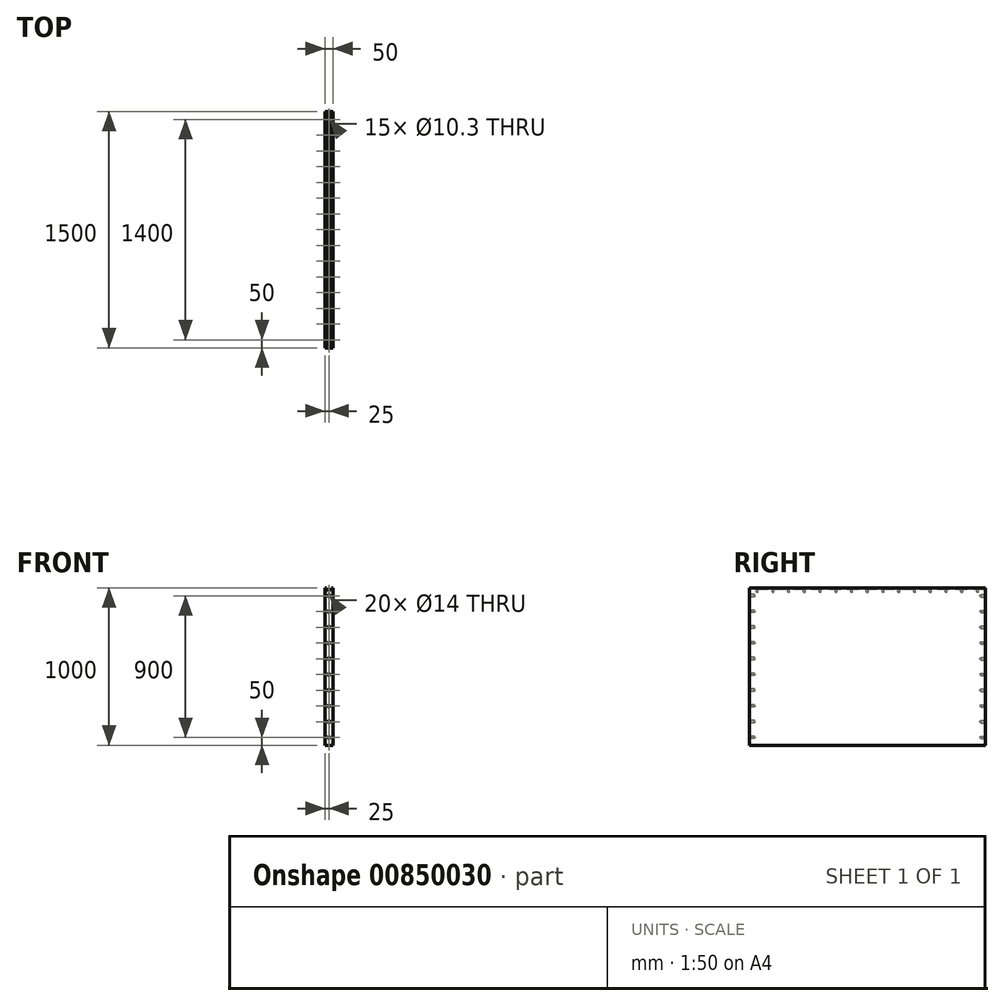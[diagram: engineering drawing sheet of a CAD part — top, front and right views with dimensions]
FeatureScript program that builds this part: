
annotation { "Feature Type Name" : "Feature", "Feature Type Description" : "" }
export const myFeature = defineFeature(function(context is Context, id is Id, definition is map)
    precondition{}
    {
        {
            var Q0;
            Q0=qCreatedBy(makeId("Right.planeOp"),FACE);
            var sketch = newSketch(context, id + "F0", { "sketchPlane" : qUnion([Q0])});
            skLineSegment(sketch, "E0.bottom", {"start": v(750, 500) * mm, "end": v(-750, 500) * mm});
            skLineSegment(sketch, "E0.top", {"start": v(750, -500) * mm, "end": v(-750, -500) * mm});
            skLineSegment(sketch, "E0.left", {"start": v(750, 500) * mm, "end": v(750, -500) * mm});
            skLineSegment(sketch, "E0.right", {"start": v(-750, 500) * mm, "end": v(-750, -500) * mm});
            skPoint(sketch, "E0.middle", {"position": v(0, 0) * mm});
            skSolve(sketch);
        }
        {
            var Q0;
            Q0=makeQuery(id+"F0.imprint","IMPRINT",FACE,{"disambiguationData":[TD([[makeQuery(id+"F0.imprint","IMPRINT",EDGE,{"derivedFrom":sQuery(id+"F0.wireOp",EDGE,"E0.bottom")}),1.0]])]});
            extrude(context, id + "F1", {"entities" : qUnion([Q0]), "depth" : 50 * mm, "offsetDistance" : 25 * mm});
        }
        {
            var Q0;
            Q0=makeQuery(id+"F1.opExtrude","SWEPT_FACE",FACE,{"disambiguationData":[OSD([sQuery(id+"F0.wireOp",EDGE,"E0.bottom")])]});
            var sketch = newSketch(context, id + "F2", { "sketchPlane" : qUnion([Q0])});
            skCircle(sketch, "E1", {"center": v(25, -700) * mm, "radius": 5.25 * mm});
            skCircle(sketch, "E2.0.1.0", {"center": v(25, -600) * mm, "radius": 5.25 * mm});
            skCircle(sketch, "E2.0.2.0", {"center": v(25, -500) * mm, "radius": 5.25 * mm});
            skCircle(sketch, "E2.0.3.0", {"center": v(25, -400) * mm, "radius": 5.25 * mm});
            skCircle(sketch, "E2.0.4.0", {"center": v(25, -300) * mm, "radius": 5.25 * mm});
            skCircle(sketch, "E2.0.5.0", {"center": v(25, -200) * mm, "radius": 5.25 * mm});
            skCircle(sketch, "E2.0.6.0", {"center": v(25, -100) * mm, "radius": 5.25 * mm});
            skCircle(sketch, "E2.0.7.0", {"center": v(25, 0) * mm, "radius": 5.25 * mm});
            skCircle(sketch, "E2.0.8.0", {"center": v(25, 100) * mm, "radius": 5.25 * mm});
            skCircle(sketch, "E2.0.9.0", {"center": v(25, 200) * mm, "radius": 5.25 * mm});
            skCircle(sketch, "E2.0.10.0", {"center": v(25, 300) * mm, "radius": 5.25 * mm});
            skCircle(sketch, "E2.0.11.0", {"center": v(25, 400) * mm, "radius": 5.25 * mm});
            skCircle(sketch, "E2.0.12.0", {"center": v(25, 500) * mm, "radius": 5.25 * mm});
            skCircle(sketch, "E2.0.13.0", {"center": v(25, 600) * mm, "radius": 5.25 * mm});
            skCircle(sketch, "E2.0.14.0", {"center": v(25, 700) * mm, "radius": 5.25 * mm});
            skLineSegment(sketch, "E2.direction1", {"start": v(25, -700) * mm, "end": v(50, -700) * mm, "construction": true});
            skLineSegment(sketch, "E2.direction2", {"start": v(25, -700) * mm, "end": v(25, -600) * mm, "construction": true});
            skSolve(sketch);
        }
        {
            var Q0;
            Q0=sQuery(id+"F2.wireOp",VERTEX,"E1.center");
            var Q1;
            Q1=sQuery(id+"F2.wireOp",VERTEX,"E2.0.1.0.center");
            var Q2;
            Q2=sQuery(id+"F2.wireOp",VERTEX,"E2.0.2.0.center");
            var Q3;
            Q3=sQuery(id+"F2.wireOp",VERTEX,"E2.0.3.0.center");
            var Q4;
            Q4=sQuery(id+"F2.wireOp",VERTEX,"E2.0.4.0.center");
            var Q5;
            Q5=sQuery(id+"F2.wireOp",VERTEX,"E2.0.5.0.center");
            var Q6;
            Q6=sQuery(id+"F2.wireOp",VERTEX,"E2.0.6.0.center");
            var Q7;
            Q7=sQuery(id+"F2.wireOp",VERTEX,"E2.0.7.0.center");
            var Q8;
            Q8=sQuery(id+"F2.wireOp",VERTEX,"E2.0.9.0.center");
            var Q9;
            Q9=sQuery(id+"F2.wireOp",VERTEX,"E2.0.8.0.center");
            var Q10;
            Q10=sQuery(id+"F2.wireOp",VERTEX,"E2.0.10.0.center");
            var Q11;
            Q11=sQuery(id+"F2.wireOp",VERTEX,"E2.0.11.0.center");
            var Q12;
            Q12=sQuery(id+"F2.wireOp",VERTEX,"E2.0.12.0.center");
            var Q13;
            Q13=sQuery(id+"F2.wireOp",VERTEX,"E2.0.14.0.center");
            var Q14;
            Q14=sQuery(id+"F2.wireOp",VERTEX,"E2.0.13.0.center");
            var Q15;
            Q15=makeQuery(id+"F1.opExtrude","SWEPT_BODY",BODY,{"disambiguationData":[OSD([sQuery(id+"F0.wireOp",EDGE,"E0.bottom"),sQuery(id+"F0.wireOp",EDGE,"E0.top"),sQuery(id+"F0.wireOp",EDGE,"E0.left"),sQuery(id+"F0.wireOp",EDGE,"E0.right")])]});
            hole(context, id + "F3", {"style" : HoleStyle.SIMPLE, "endStyle" : HoleEndStyle.BLIND, "standardTappedOrClearance" : lookupTablePath({ "standard" : "ISO", "fit" : "Normal", "engagement" : "75%", "pitch" : "1.75 mm", "size" : "M12", "type" : "Tapped" }), "standardBlindInLast" : lookupTablePath({ "fit" : "Standard", "standard" : "ISO", "engagement" : "75%", "pitch" : "1.75 mm", "size" : "M12", "type" : "Tapped" }), "holeDiameter" : 10.3 * mm, "majorDiameter" : 12 * mm, "showTappedDepth" : true, "holeDepth" : 25.25 * mm, "isTappedThrough" : true, "tappedDepth" : 20 * mm, "tapClearance" : 3, "locations" : qUnion([Q0, Q1, Q2, Q3, Q4, Q5, Q6, Q7, Q8, Q9, Q10, Q11, Q12, Q13, Q14]), "scope" : qUnion([Q15])});
        }
        {
            var Q0;
            Q0=makeQuery(id+"F1.opExtrude","SWEPT_FACE",FACE,{"disambiguationData":[OSD([sQuery(id+"F0.wireOp",EDGE,"E0.right")])]});
            var sketch = newSketch(context, id + "F4", { "sketchPlane" : qUnion([Q0])});
            skLineSegment(sketch, "E3.bottom", {"start": v(40, 490) * mm, "end": v(10, 490) * mm});
            skLineSegment(sketch, "E3.top", {"start": v(40, 510) * mm, "end": v(10, 510) * mm});
            skLineSegment(sketch, "E3.left", {"start": v(40, 490) * mm, "end": v(40, 510) * mm});
            skLineSegment(sketch, "E3.right", {"start": v(10, 490) * mm, "end": v(10, 510) * mm});
            skPoint(sketch, "E3.middle", {"position": v(25, 500) * mm});
            skSolve(sketch);
        }
        {
            var Q0;
            {var subQ0=sQuery(id+"F4.wireOp",EDGE,"E3.bottom");Q0=makeQuery(id+"F4.imprint","IMPRINT",FACE,{"disambiguationData":[TD([[makeQuery(id+"F4.imprint","IMPRINT",EDGE,{"derivedFrom":subQ0}),-1.0]])]});}
            extrude(context, id + "F5", {"entities" : qUnion([Q0]), "operationType" : NewBodyOperationType.REMOVE, "endBound" : BoundingType.THROUGH_ALL, "oppositeDirection" : true, "depth" : 25 * mm, "offsetDistance" : 25 * mm});
        }
        {
            var Q0;
            Q0=makeQuery(id+"F1.opExtrude","SWEPT_FACE",FACE,{"disambiguationData":[OSD([sQuery(id+"F0.wireOp",EDGE,"E0.right")])]});
            var sketch = newSketch(context, id + "F6", { "sketchPlane" : qUnion([Q0])});
            skCircle(sketch, "E4", {"center": v(25, -450) * mm, "radius": 7 * mm});
            skPoint(sketch, "E4.centerSnap0", {"position": v(25, -500) * mm});
            skCircle(sketch, "E5.0.1.0", {"center": v(25, -350) * mm, "radius": 7 * mm});
            skCircle(sketch, "E5.0.2.0", {"center": v(25, -250) * mm, "radius": 7 * mm});
            skCircle(sketch, "E5.0.3.0", {"center": v(25, -150) * mm, "radius": 7 * mm});
            skCircle(sketch, "E5.0.4.0", {"center": v(25, -50) * mm, "radius": 7 * mm});
            skCircle(sketch, "E5.0.5.0", {"center": v(25, 50) * mm, "radius": 7 * mm});
            skCircle(sketch, "E5.0.6.0", {"center": v(25, 150) * mm, "radius": 7 * mm});
            skCircle(sketch, "E5.0.7.0", {"center": v(25, 250) * mm, "radius": 7 * mm});
            skCircle(sketch, "E5.0.8.0", {"center": v(25, 350) * mm, "radius": 7 * mm});
            skCircle(sketch, "E5.0.9.0", {"center": v(25, 450) * mm, "radius": 7 * mm});
            skLineSegment(sketch, "E5.direction1", {"start": v(25, -450) * mm, "end": v(140, -450) * mm, "construction": true});
            skLineSegment(sketch, "E5.direction2", {"start": v(25, -450) * mm, "end": v(25, -350) * mm, "construction": true});
            skSolve(sketch);
        }
        {
            var Q0;
            Q0=sQuery(id+"F6.wireOp",VERTEX,"E5.direction1.start");
            var Q1;
            Q1=sQuery(id+"F6.wireOp",VERTEX,"E5.direction2.end");
            var Q2;
            Q2=sQuery(id+"F6.wireOp",VERTEX,"E5.0.2.0.center");
            var Q3;
            Q3=sQuery(id+"F6.wireOp",VERTEX,"E5.0.3.0.center");
            var Q4;
            Q4=sQuery(id+"F6.wireOp",VERTEX,"E5.0.4.0.center");
            var Q5;
            Q5=sQuery(id+"F6.wireOp",VERTEX,"E5.0.5.0.center");
            var Q6;
            Q6=sQuery(id+"F6.wireOp",VERTEX,"E5.0.9.0.center");
            var Q7;
            Q7=sQuery(id+"F6.wireOp",VERTEX,"E5.0.8.0.center");
            var Q8;
            Q8=sQuery(id+"F6.wireOp",VERTEX,"E5.0.7.0.center");
            var Q9;
            Q9=sQuery(id+"F6.wireOp",VERTEX,"E5.0.6.0.center");
            var Q10;
            Q10=makeQuery(id+"F1.opExtrude","SWEPT_BODY",BODY,{"disambiguationData":[OSD([sQuery(id+"F0.wireOp",EDGE,"E0.bottom"),sQuery(id+"F0.wireOp",EDGE,"E0.top"),sQuery(id+"F0.wireOp",EDGE,"E0.left"),sQuery(id+"F0.wireOp",EDGE,"E0.right")])]});
            hole(context, id + "F7", {"style" : HoleStyle.SIMPLE, "endStyle" : HoleEndStyle.BLIND, "standardTappedOrClearance" : lookupTablePath({ "standard" : "ISO", "engagement" : "75%", "pitch" : "2 mm", "size" : "M16", "type" : "Tapped" }), "standardBlindInLast" : lookupTablePath({ "standard" : "ISO", "engagement" : "75%", "pitch" : "2 mm", "size" : "M16", "type" : "Tapped" }), "holeDiameter" : 14 * mm, "majorDiameter" : 16 * mm, "showTappedDepth" : true, "holeDepth" : 31 * mm, "isTappedThrough" : true, "tappedDepth" : 25 * mm, "tapClearance" : 3, "startFromSketch" : true, "locations" : qUnion([Q0, Q1, Q2, Q3, Q4, Q5, Q6, Q7, Q8, Q9]), "scope" : qUnion([Q10])});
        }
        {
            var Q0;
            Q0=makeQuery(id+"F1.opExtrude","SWEPT_FACE",FACE,{"disambiguationData":[OSD([sQuery(id+"F0.wireOp",EDGE,"E0.left")])]});
            var sketch = newSketch(context, id + "F8", { "sketchPlane" : qUnion([Q0])});
            skCircle(sketch, "E6", {"center": v(-25, -450) * mm, "radius": 7 * mm});
            skCircle(sketch, "E7.0.1.0", {"center": v(-25, -350) * mm, "radius": 7 * mm});
            skCircle(sketch, "E7.0.2.0", {"center": v(-25, -250) * mm, "radius": 7 * mm});
            skCircle(sketch, "E7.0.3.0", {"center": v(-25, -150) * mm, "radius": 7 * mm});
            skCircle(sketch, "E7.0.4.0", {"center": v(-25, -50) * mm, "radius": 7 * mm});
            skCircle(sketch, "E7.0.5.0", {"center": v(-25, 50) * mm, "radius": 7 * mm});
            skCircle(sketch, "E7.0.6.0", {"center": v(-25, 150) * mm, "radius": 7 * mm});
            skCircle(sketch, "E7.0.7.0", {"center": v(-25, 250) * mm, "radius": 7 * mm});
            skCircle(sketch, "E7.0.8.0", {"center": v(-25, 350) * mm, "radius": 7 * mm});
            skCircle(sketch, "E7.0.9.0", {"center": v(-25, 450) * mm, "radius": 7 * mm});
            skLineSegment(sketch, "E7.direction1", {"start": v(-25, -450) * mm, "end": v(0, -450) * mm, "construction": true});
            skLineSegment(sketch, "E7.direction2", {"start": v(-25, -450) * mm, "end": v(-25, -350) * mm, "construction": true});
            skSolve(sketch);
        }
        {
            var Q0;
            Q0=sQuery(id+"F8.wireOp",VERTEX,"E7.0.9.0.center");
            var Q1;
            Q1=sQuery(id+"F8.wireOp",VERTEX,"E7.0.8.0.center");
            var Q2;
            Q2=sQuery(id+"F8.wireOp",VERTEX,"E7.0.7.0.center");
            var Q3;
            Q3=sQuery(id+"F8.wireOp",VERTEX,"E7.0.6.0.center");
            var Q4;
            Q4=sQuery(id+"F8.wireOp",VERTEX,"E7.0.5.0.center");
            var Q5;
            Q5=sQuery(id+"F8.wireOp",VERTEX,"E7.0.4.0.center");
            var Q6;
            Q6=sQuery(id+"F8.wireOp",VERTEX,"E7.0.3.0.center");
            var Q7;
            Q7=sQuery(id+"F8.wireOp",VERTEX,"E7.0.2.0.center");
            var Q8;
            Q8=sQuery(id+"F8.wireOp",VERTEX,"E7.direction2.end");
            var Q9;
            Q9=sQuery(id+"F8.wireOp",VERTEX,"E7.direction1.start");
            var Q10;
            Q10=makeQuery(id+"F1.opExtrude","SWEPT_BODY",BODY,{"disambiguationData":[OSD([sQuery(id+"F0.wireOp",EDGE,"E0.bottom"),sQuery(id+"F0.wireOp",EDGE,"E0.top"),sQuery(id+"F0.wireOp",EDGE,"E0.left"),sQuery(id+"F0.wireOp",EDGE,"E0.right")])]});
            hole(context, id + "F9", {"style" : HoleStyle.SIMPLE, "endStyle" : HoleEndStyle.BLIND, "standardTappedOrClearance" : lookupTablePath({ "standard" : "ISO", "engagement" : "75%", "pitch" : "2 mm", "size" : "M16", "type" : "Tapped" }), "standardBlindInLast" : lookupTablePath({ "standard" : "ISO", "engagement" : "75%", "pitch" : "2 mm", "size" : "M16", "type" : "Tapped" }), "holeDiameter" : 14 * mm, "majorDiameter" : 16 * mm, "showTappedDepth" : true, "holeDepth" : 31 * mm, "isTappedThrough" : true, "tappedDepth" : 25 * mm, "tapClearance" : 3, "startFromSketch" : true, "locations" : qUnion([Q0, Q1, Q2, Q3, Q4, Q5, Q6, Q7, Q8, Q9]), "scope" : qUnion([Q10])});
        }
    });
